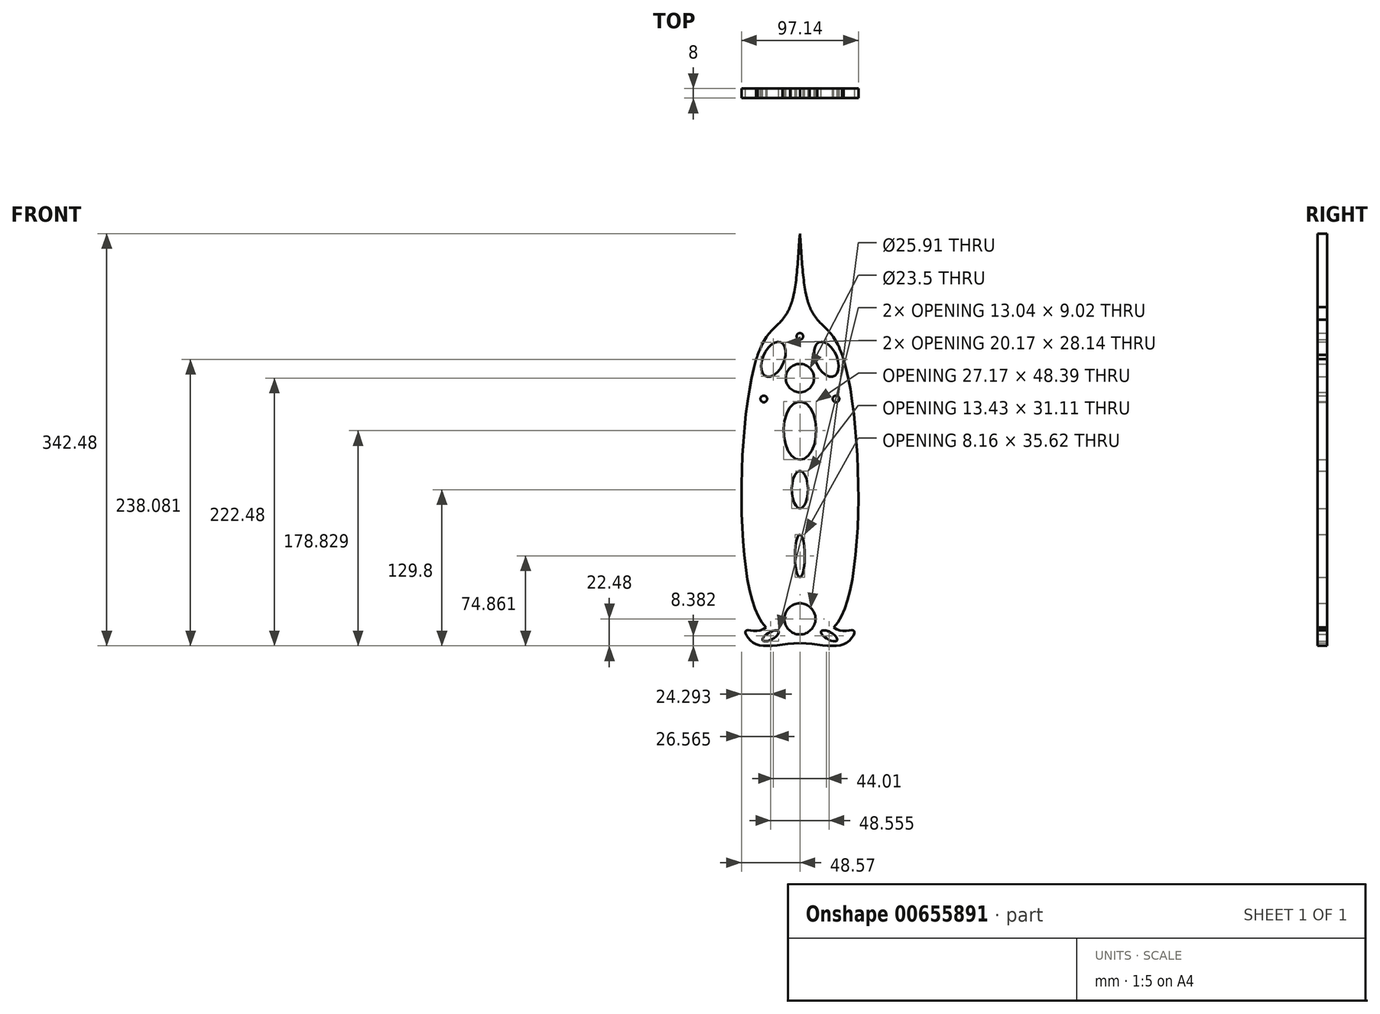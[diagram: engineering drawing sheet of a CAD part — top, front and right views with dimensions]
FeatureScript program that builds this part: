
annotation { "Feature Type Name" : "Feature", "Feature Type Description" : "" }
export const myFeature = defineFeature(function(context is Context, id is Id, definition is map)
    precondition{}
    {
        {
            var Q0;
            Q0=qCreatedBy(makeId("Front.planeOp"),FACE);
            var sketch = newSketch(context, id + "F0", { "sketchPlane" : qUnion([Q0])});
            skCircle(sketch, "E0", {"center": v(0, 220) * mm, "radius": 11.75 * mm});
            skLineSegment(sketch, "E1.trimOffspring", {"start": v(143.56, 0) * mm, "end": v(150, 0) * mm});
            skCircle(sketch, "E2", {"center": v(0, 254.64) * mm, "radius": 2.75 * mm});
            skCircle(sketch, "E3", {"center": v(-30, 202.68) * mm, "radius": 2.75 * mm});
            skCircle(sketch, "E4", {"center": v(30, 202.68) * mm, "radius": 2.75 * mm});
            skPoint(sketch, "E5.1.internal.orphan", {"position": v(-5, 290) * mm});
            skPoint(sketch, "E6.0.internal.orphan", {"position": v(0, 340) * mm});
            skPoint(sketch, "E6.1.internal.orphan", {"position": v(5, 290) * mm});
            skPoint(sketch, "E6.endDerivative.orphan", {"position": v(143.56, 0) * mm});
            skPoint(sketch, "E7.start.orphan", {"position": v(-150, 0) * mm});
            skPoint(sketch, "E8.end.orphan", {"position": v(21.71, 0) * mm});
            skPoint(sketch, "E8.start.orphan", {"position": v(-21.71, 0) * mm});
            skFitSpline(sketch, "E9", {"points": [v(0, 340) * mm, v(5, 290) * mm, v(14.4, 268.6) * mm, v(35, 239.36) * mm, v(35, 23.08) * mm, v(0, 0) * mm], "startDerivative": vector(22.83, -298.86) * mm, "endDerivative": vector(-227.21, -67.5) * mm});
            skFitSpline(sketch, "E10", {"points": [v(0, 340) * mm, v(-5, 290) * mm, v(-14.4, 268.6) * mm, v(-35, 239.36) * mm, v(-35, 23.08) * mm, v(0, 0) * mm], "startDerivative": vector(-22.83, -298.86) * mm, "endDerivative": vector(227.21, -67.5) * mm});
            skLineSegment(sketch, "E11", {"start": v(0, 340) * mm, "end": v(0, 0) * mm});
            skFitSpline(sketch, "E12", {"points": [v(5, 290) * mm, v(14.4, 268.6) * mm, v(35, 239.36) * mm, v(35, 184.3) * mm, v(19.6, 161.76) * mm, v(14.4, 40.08) * mm, v(35, 10) * mm, v(45, 10) * mm, v(38.7, 0) * mm, v(0, 0) * mm], "startDerivative": vector(54.27, -286.4) * mm, "endDerivative": vector(-440.53, 24.07) * mm});
            skFitSpline(sketch, "E13", {"points": [v(-5, 290) * mm, v(-14.4, 268.6) * mm, v(-35, 239.36) * mm, v(-35, 184.3) * mm, v(-19.6, 161.76) * mm, v(-14.4, 40.08) * mm, v(-35, 10) * mm, v(-45, 10) * mm, v(-38.7, 0) * mm, v(0, 0) * mm], "startDerivative": vector(-54.27, -286.4) * mm, "endDerivative": vector(440.53, 24.07) * mm});
            skCircle(sketch, "E14", {"center": v(0, 20) * mm, "radius": 12.96 * mm});
            skEllipse(sketch, "E15", {"center": v(0, 176.35) * mm, "majorRadius": 24.2 * mm, "minorRadius": 13.58 * mm, "majorAxis": v(0, -1)});
            skEllipse(sketch, "E16", {"center": v(24.28, 5.9) * mm, "majorRadius": 7.53 * mm, "minorRadius": 3.02 * mm, "majorAxis": v(0.87, -0.5)});
            skEllipse(sketch, "E17", {"center": v(-24.28, 5.9) * mm, "majorRadius": 7.53 * mm, "minorRadius": 3.02 * mm, "majorAxis": v(0.87, 0.5)});
            skEllipse(sketch, "E18", {"center": v(0, 127.32) * mm, "majorRadius": 15.55 * mm, "minorRadius": 6.71 * mm, "majorAxis": v(0, -1)});
            skEllipse(sketch, "E19", {"center": v(0, 72.38) * mm, "majorRadius": 17.81 * mm, "minorRadius": 4.08 * mm, "majorAxis": v(0, 1)});
            skEllipse(sketch, "E20", {"center": v(-22, 235.6) * mm, "majorRadius": 15.37 * mm, "minorRadius": 8.82 * mm, "majorAxis": v(0.4, 0.92)});
            skEllipse(sketch, "E21", {"center": v(22, 235.6) * mm, "majorRadius": 15.37 * mm, "minorRadius": 8.82 * mm, "majorAxis": v(-0.4, 0.92)});
            skSolve(sketch);
        }
        {
            var Q0;
            Q0 = qSketchRegion(id + "F0", true);
            extrude(context, id + "F1", {"entities" : qUnion([Q0]), "flatOperationType" : FlatOperationType.REMOVE, "depth" : 8 * mm, "offsetDistance" : 25 * mm, "domain" : OperationDomain.MODEL});
        }
    });
